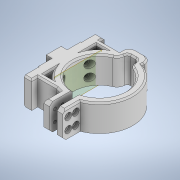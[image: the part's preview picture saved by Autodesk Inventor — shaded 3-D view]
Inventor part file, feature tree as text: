
AUTODESK INVENTOR PART (.ipt)
format: ipt  version: 2020 (Build 240168000, 168)  size: 455,680 bytes
history: native  units: mm
features: extrude x16, sketch x16, fillet x2, chamfer x2, other x1
ambient origin geometry x8: Origin, YZ Plane, XZ Plane, XY Plane, X Axis, Y Axis, Z Axis, Center Point
bodies: Solide1 (feature_tree)
feature tree (37):
  extrude  "Extrusion1"  Depth=88.4mm
  extrude  "Extrusion2"  Depth=35.0mm TaperAngle=0.0deg
  extrude  "Extrusion3"  Depth=68.5mm
  extrude  "Extrusion4"  TaperAngle=0.0deg  [1 undecoded]
  fillet  "Congé1"  Radius=20.0mm
  fillet  "Congé2"  Radius=30.0mm
  extrude  "Extrusion5"  Depth=15.0mm
  extrude  "Extrusion6"  Depth=9.95mm
  extrude  "Extrusion7"  Depth=35.0mm TaperAngle=0.0deg
  chamfer  "Chanfrein1"  Distance=15.0mm
  extrude  "Extrusion8"  Depth=15.0mm
  extrude  "Extrusion9"  Depth=7.5mm
  extrude  "Extrusion10"  Depth=10.0mm
  extrude  "Extrusion11"  Depth=35.0mm TaperAngle=0.0deg
  extrude  "Extrusion12"  Depth=10.0mm
  extrude  "Extrusion13"  Depth=4.0mm
  extrude  "Extrusion14"  Depth=30.0mm
  other  "Plan de construction2"
  extrude  "Extrusion15"  Depth=25.0mm
  chamfer  "Chanfrein2"  Distance=12.5mm
  extrude  "Extrusion16"  Depth=35.0mm TaperAngle=0.0deg
  sketch  "Esquisse1"
  sketch  "Esquisse2"
  sketch  "Esquisse3"
  sketch  "Esquisse4"
  sketch  "Esquisse5"
  sketch  "Esquisse6"
  sketch  "Esquisse7"
  sketch  "Esquisse10"
  sketch  "Esquisse11"
  sketch  "Esquisse12"
  sketch  "Esquisse13"
  sketch  "Esquisse14"
  sketch  "Esquisse15"
  sketch  "Esquisse16"
  sketch  "Esquisse19"
  sketch  "Esquisse20"
note: 1 required parameter value undecoded (feature->parameter linkage not recoverable at this tier; creation-order binding heuristic only, values carry confidence <= 0.55)
